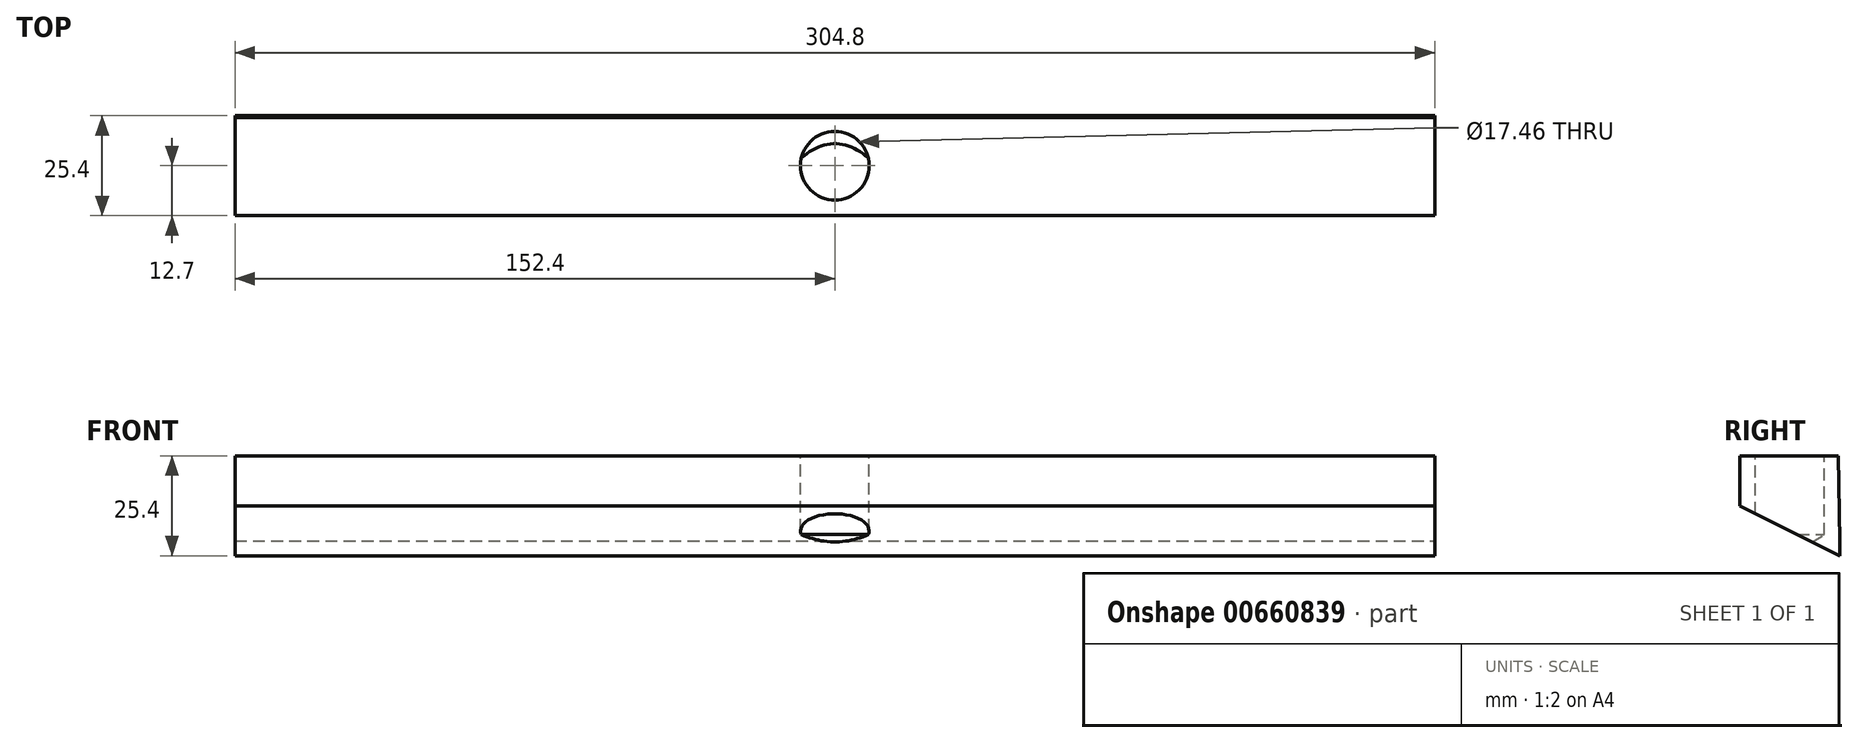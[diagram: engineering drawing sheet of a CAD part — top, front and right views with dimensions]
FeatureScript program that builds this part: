
annotation { "Feature Type Name" : "Feature", "Feature Type Description" : "" }
export const myFeature = defineFeature(function(context is Context, id is Id, definition is map)
    precondition{}
    {
        {
            var Q0;
            Q0=qCreatedBy(makeId("Right.planeOp"),FACE);
            var sketch = newSketch(context, id + "F0", { "sketchPlane" : qUnion([Q0])});
            skLineSegment(sketch, "E0.bottom", {"start": v(-12.7, 12.7) * mm, "end": v(12.7, 12.7) * mm});
            skLineSegment(sketch, "E0.top", {"start": v(-12.7, -12.7) * mm, "end": v(12.7, -12.7) * mm});
            skLineSegment(sketch, "E0.left", {"start": v(-12.7, 12.7) * mm, "end": v(-12.7, -12.7) * mm});
            skLineSegment(sketch, "E0.right", {"start": v(12.7, 12.7) * mm, "end": v(12.7, -12.7) * mm});
            skSolve(sketch);
        }
        {
            var Q0;
            Q0=makeQuery(id+"F0.imprint","IMPRINT",FACE,{"disambiguationData":[TD([[makeQuery(id+"F0.imprint","IMPRINT",EDGE,{"derivedFrom":sQuery(id+"F0.wireOp",EDGE,"E0.bottom")}),-1.0]])]});
            extrude(context, id + "F1", {"entities" : qUnion([Q0]), "endBound" : BoundingType.SYMMETRIC, "depth" : 304.8 * mm, "offsetDistance" : 25.4 * mm});
        }
        {
            var Q0;
            Q0=makeQuery(id+"F1.opExtrude","SWEPT_FACE",FACE,{"disambiguationData":[OSD([sQuery(id+"F0.wireOp",EDGE,"E0.bottom")])]});
            var sketch = newSketch(context, id + "F2", { "sketchPlane" : qUnion([Q0])});
            skPoint(sketch, "E1", {"position": v(0, 0) * mm});
            skSolve(sketch);
        }
        {
            var Q0;
            Q0=sQuery(id+"F2.wireOp",VERTEX,"E1");
            var Q1;
            Q1=makeQuery(id+"F1.opExtrude","SWEPT_BODY",BODY,{"disambiguationData":[OSD([sQuery(id+"F0.wireOp",EDGE,"E0.bottom"),sQuery(id+"F0.wireOp",EDGE,"E0.top"),sQuery(id+"F0.wireOp",EDGE,"E0.left"),sQuery(id+"F0.wireOp",EDGE,"E0.right")])]});
            hole(context, id + "F3", {"style" : HoleStyle.SIMPLE, "endStyle" : HoleEndStyle.BLIND, "standardTappedOrClearance" : lookupTablePath({ "standard" : "ANSI", "engagement" : "75%", "pitch" : "16 tpi", "size" : "3/4", "type" : "Tapped" }), "standardBlindInLast" : lookupTablePath({ "standard" : "ANSI", "engagement" : "75%", "pitch" : "16 tpi", "size" : "3/4", "type" : "Tapped" }), "holeDiameter" : 17.46 * mm, "majorDiameter" : 19.05 * mm, "showTappedDepth" : true, "holeDepth" : 20 * mm, "isTappedThrough" : true, "tappedDepth" : 15.24 * mm, "tapClearance" : 3, "locations" : qUnion([Q0]), "scope" : qUnion([Q1])});
        }
        {
            var Q0;
            Q0=makeQuery(id+"F1.opExtrude","CAP_FACE",FACE,{"disambiguationData":[OSD([sQuery(id+"F0.wireOp",EDGE,"E0.bottom"),sQuery(id+"F0.wireOp",EDGE,"E0.top"),sQuery(id+"F0.wireOp",EDGE,"E0.left"),sQuery(id+"F0.wireOp",EDGE,"E0.right")])],"isStart":false});
            var sketch = newSketch(context, id + "F4", { "sketchPlane" : qUnion([Q0])});
            skLineSegment(sketch, "E2.0", {"start": v(-12.7, 0) * mm, "end": v(-12.7, -12.7) * mm});
            skLineSegment(sketch, "E3.0", {"start": v(-12.7, -12.7) * mm, "end": v(12.7, -12.7) * mm});
            skLineSegment(sketch, "E4", {"start": v(12.7, -12.7) * mm, "end": v(-12.7, 0) * mm});
            skPoint(sketch, "E5.orphan", {"position": v(-12.7, 12.7) * mm});
            skSolve(sketch);
        }
        {
            var Q0;
            Q0 = qSketchRegion(id + "F4", true);
            extrude(context, id + "F5", {"entities" : qUnion([Q0]), "operationType" : NewBodyOperationType.REMOVE, "endBound" : BoundingType.THROUGH_ALL, "oppositeDirection" : true, "depth" : 25.4 * mm, "offsetDistance" : 25.4 * mm});
        }
        {
            var Q0;
            Q0=makeQuery(id+"F1.opExtrude","CAP_FACE",FACE,{"disambiguationData":[OSD([sQuery(id+"F0.wireOp",EDGE,"E0.bottom"),sQuery(id+"F0.wireOp",EDGE,"E0.top"),sQuery(id+"F0.wireOp",EDGE,"E0.left"),sQuery(id+"F0.wireOp",EDGE,"E0.right")])],"isStart":false});
            var sketch = newSketch(context, id + "F6", { "sketchPlane" : qUnion([Q0])});
            skLineSegment(sketch, "E6", {"start": v(12.7, -8.89) * mm, "end": v(12.23, 12.7) * mm});
            skLineSegment(sketch, "E7", {"start": v(12.23, 12.7) * mm, "end": v(12.7, 12.7) * mm});
            skLineSegment(sketch, "E8", {"start": v(12.7, 12.7) * mm, "end": v(12.7, -8.89) * mm});
            skSolve(sketch);
        }
        {
            var Q0;
            Q0 = qSketchRegion(id + "F6", true);
            extrude(context, id + "F7", {"entities" : qUnion([Q0]), "operationType" : NewBodyOperationType.REMOVE, "endBound" : BoundingType.THROUGH_ALL, "oppositeDirection" : true, "depth" : 25.4 * mm, "offsetDistance" : 25.4 * mm});
        }
    });
